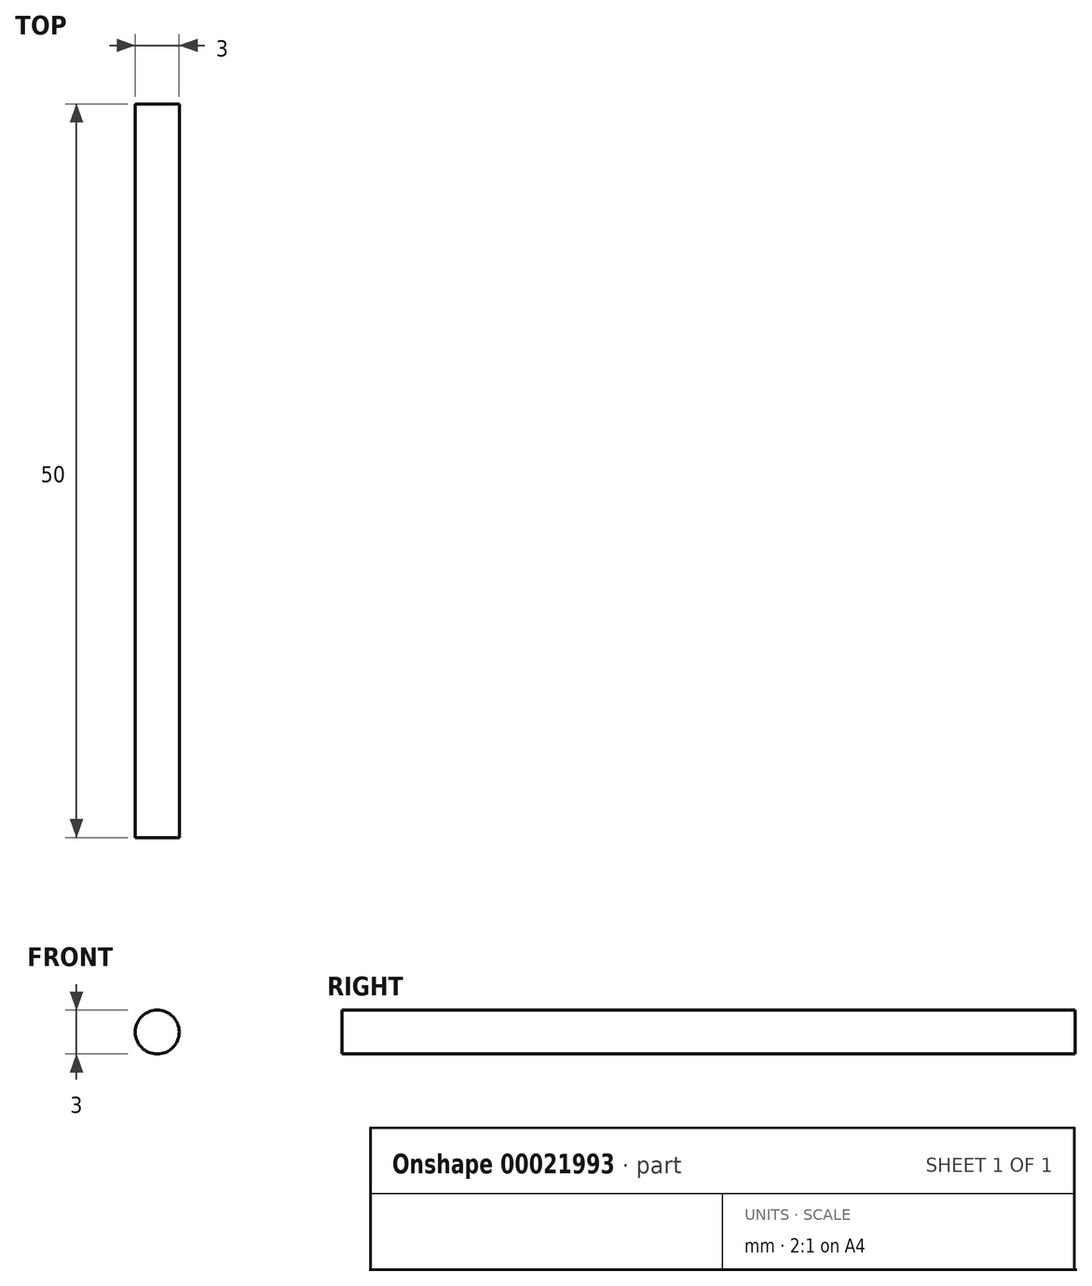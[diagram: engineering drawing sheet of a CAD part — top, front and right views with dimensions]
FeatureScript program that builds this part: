
annotation { "Feature Type Name" : "Feature", "Feature Type Description" : "" }
export const myFeature = defineFeature(function(context is Context, id is Id, definition is map)
    precondition{}
    {
        {
            var Q0;
            Q0=qCreatedBy(makeId("Front.planeOp"),FACE);
            var sketch = newSketch(context, id + "F0", { "sketchPlane" : qUnion([Q0])});
            skCircle(sketch, "E0", {"center": v(-56.6, -28.89) * mm, "radius": 1.5 * mm});
            skSolve(sketch);
        }
        {
            var Q0;
            Q0=makeQuery(id+"F0.imprint","IMPRINT",FACE,{"disambiguationData":[TD([[makeQuery(id+"F0.imprint","IMPRINT",EDGE,{"derivedFrom":sQuery(id+"F0.wireOp",EDGE,"E0")}),1.0]])]});
            extrude(context, id + "F1", {"entities" : qUnion([Q0]), "depth" : 50 * mm});
        }
    });
